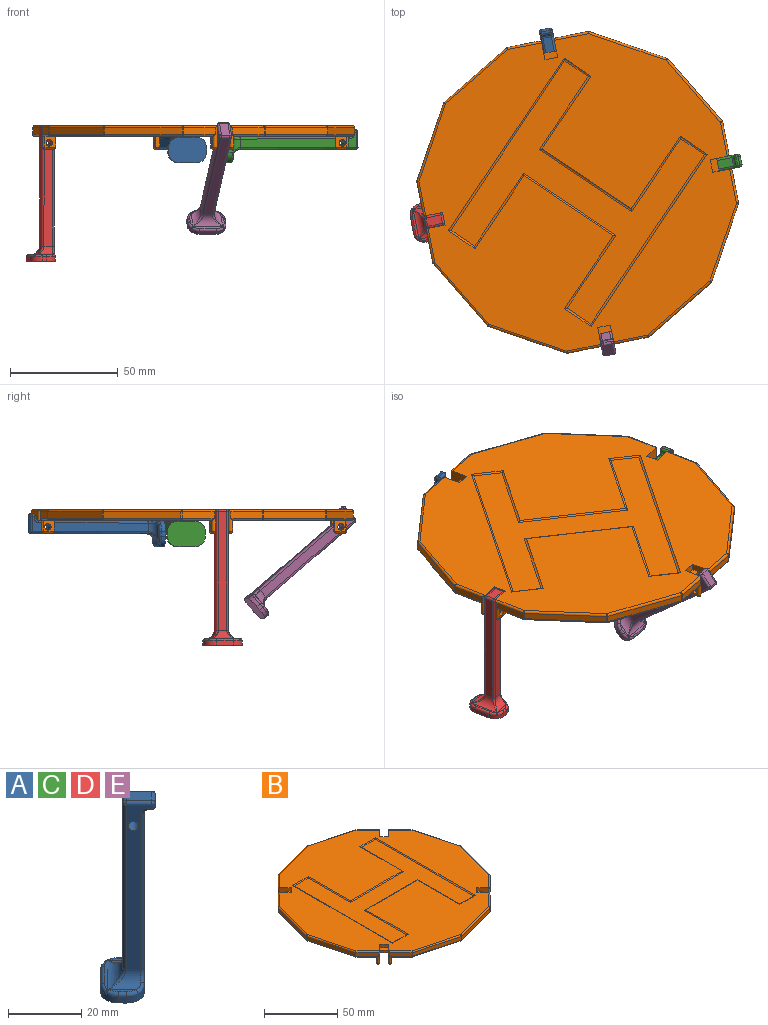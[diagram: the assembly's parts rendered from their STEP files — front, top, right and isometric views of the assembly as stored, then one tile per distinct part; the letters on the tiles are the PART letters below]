
ASSEMBLY  parts=5 mates=4
PART A: 63 faces, bbox 17.9x17.9x63 mm
  f0: plane 9.4x9.4mm, normal (0,0,1), area 11.6mm2, adj f20,f30,f34,f40
  f1: plane 5.16x5.16mm, normal (0,0,1), area 5.6mm2, adj f21,f54,f57,f59
  f2: plane 3.54x3.54mm, normal (0,0,-1), area 4mm2, adj f48,f49,f55,f56
  f3: plane 55x4.95mm, normal (-0.71,-0.71,0), area 216.8mm2, adj f9,f21,f36,f41,f47,f55,f58,f60
  f4: plane 7.78x7.78mm, normal (0,0,1), area 28mm2, adj f28,f31,f36,f37
  f5: plane 2.83x2.83mm, normal (0.71,-0.71,0), area 4mm2, adj f37,f38,f47,f48
  f6: plane 55x4.95mm, normal (0.71,0.71,0), area 216.8mm2, adj f9,f19,f24,f28,f38,f49,f50,f53
  f7: plane 55x2.83mm, normal (-0.71,0.71,0), area 220mm2, adj f20,f24,f31,f41
  f8: plane 59x5.66mm, normal (0.71,-0.71,0), area 252.8mm2, adj f10,f16,f17,f44,f50,f56,f60,f62
  f9: cylinder r=1.5mm len=6.36mm, axis (-0.71,-0.71,0), area 56.5mm2, adj f3,f6
  f10: cylinder r=5mm len=7.07mm, axis (0,0,1), area 17.8mm2, adj f8,f11,f17,f59,f61
  f11: plane 2x1.41mm, normal (-0.71,-0.71,0), area 4mm2, adj f10,f12,f17,f57
  f12: cylinder r=5mm len=7.07mm, axis (0,0,1), area 15.7mm2, adj f11,f13,f17,f40,f45,f51,f54
  f13: plane 5.66x5.66mm, normal (-0.71,0.71,0), area 16mm2, adj f12,f14,f17,f34
  f14: cylinder r=5mm len=7.07mm, axis (0,0,1), area 15.7mm2, adj f13,f15,f17,f22,f25,f26,f30
  f15: plane 2x1.41mm, normal (0.71,0.71,0), area 4mm2, adj f14,f16,f17,f29
  f16: cylinder r=5mm len=7.07mm, axis (0,0,1), area 17.8mm2, adj f8,f15,f17,f33,f39
  f17: plane 17.07x17.07mm, normal (0,0,-1), area 194.5mm2, adj f8,f10,f11,f12,f13,f14,f15,f16
  f18: plane 5.16x5.16mm, normal (0,0,1), area 5.6mm2, adj f19,f25,f29,f33
  f19: cylinder r=4mm len=9.07mm, axis (0.71,-0.71,0), area 35.5mm2, adj f6,f18,f22,f23,f39,f44
  f20: cylinder r=4mm len=12.49mm, axis (0.71,0.71,0), area 47.9mm2, adj f0,f7,f23,f26,f45,f46
  f21: cylinder r=4mm len=9.07mm, axis (-0.71,0.71,0), area 35.5mm2, adj f1,f3,f46,f51,f61,f62
  f22: bspline ~1.31x1.14mm, area 0.4mm2, adj f14,f19,f23,f25,f26
  f23: bspline ~6.36x4.13mm, area 7.1mm2, adj f19,f20,f22,f24,f26
  f24: cylinder r=1mm len=55mm, axis (0,0,1), area 86.4mm2, adj f6,f7,f23,f27
  f25: torus R=4mm, axis (0,0,-1), area 5.3mm2, adj f14,f18,f22,f29
  f26: bspline ~2.07x1.24mm, area 0.5mm2, adj f14,f20,f22,f23,f30
  f27: sphere r=1mm, area 1.9mm2, adj f24,f28,f31
  f28: cylinder r=1mm len=5.66mm, axis (-0.71,0.71,0), area 11mm2, adj f4,f6,f27,f32
  f29: cylinder r=1mm len=2.12mm, axis (0.71,-0.71,0), area 3.1mm2, adj f15,f18,f25,f33
  f30: torus R=4mm, axis (0,0,-1), area 5.3mm2, adj f0,f14,f26,f34
  f31: cylinder r=1mm len=3.54mm, axis (-0.71,-0.71,0), area 6.3mm2, adj f4,f7,f27,f35
  f32: sphere r=1mm, area 1.6mm2, adj f28,f37,f38
  f33: torus R=4mm, axis (0,0,-1), area 5.3mm2, adj f16,f18,f29,f39
  f34: cylinder r=1mm len=6.36mm, axis (0.71,0.71,0), area 12.6mm2, adj f0,f13,f30,f40
  f35: sphere r=1mm, area 1mm2, adj f31,f36,f41
  f36: cylinder r=1mm len=5.66mm, axis (0.71,-0.71,0), area 11mm2, adj f3,f4,f35,f42
  f37: cylinder r=1mm len=3.54mm, axis (0.71,0.71,0), area 6.3mm2, adj f4,f5,f32,f42
  f38: cylinder r=1mm len=1.41mm, axis (0,0,-1), area 1.6mm2, adj f5,f6,f32,f43
  f39: bspline ~5.56x2.46mm, area 5.6mm2, adj f16,f19,f33,f44
  f40: torus R=4mm, axis (0,0,-1), area 5.3mm2, adj f0,f12,f34,f45
  f41: cylinder r=1mm len=55mm, axis (0,0,-1), area 86.4mm2, adj f3,f7,f35,f46
  f42: sphere r=1mm, area 1.6mm2, adj f36,f37,f47
  f43: sphere r=1mm, area 1.3mm2, adj f38,f48,f49
  f44: torus R=5mm, axis (-0.71,0.71,0), area 6.4mm2, adj f8,f19,f39,f50
  f45: bspline ~1.31x1.14mm, area 0.4mm2, adj f12,f20,f40,f46,f51
  f46: bspline ~6.36x4.13mm, area 7.1mm2, adj f20,f21,f41,f45,f51
  f47: cylinder r=1mm len=1.41mm, axis (0,0,1), area 1.6mm2, adj f3,f5,f42,f52
  f48: cylinder r=1mm len=3.54mm, axis (0.71,0.71,0), area 6.3mm2, adj f2,f5,f43,f52
  f49: cylinder r=1mm len=1.41mm, axis (-0.71,0.71,0), area 1.6mm2, adj f2,f6,f43,f53
  f50: cylinder r=1mm len=52mm, axis (0,0,1), area 81.7mm2, adj f6,f8,f44,f53
  f51: bspline ~2.07x1.24mm, area 0.5mm2, adj f12,f21,f45,f46,f54
  f52: sphere r=1mm, area 1mm2, adj f47,f48,f55
  f53: torus R=2mm, axis (-0.71,-0.71,0), area 3.4mm2, adj f6,f49,f50,f56
  f54: torus R=4mm, axis (0,0,-1), area 5.3mm2, adj f1,f12,f51,f57
  f55: cylinder r=1mm len=1.41mm, axis (0.71,-0.71,0), area 1.6mm2, adj f2,f3,f52,f58
  f56: cylinder r=1mm len=3.54mm, axis (-0.71,-0.71,0), area 6.3mm2, adj f2,f8,f53,f58
  f57: cylinder r=1mm len=2.12mm, axis (-0.71,0.71,0), area 3.1mm2, adj f1,f11,f54,f59
  f58: torus R=2mm, axis (-0.71,-0.71,0), area 3.4mm2, adj f3,f55,f56,f60
  f59: torus R=4mm, axis (0,0,-1), area 5.3mm2, adj f1,f10,f57,f61
  f60: cylinder r=1mm len=52mm, axis (0,0,-1), area 81.7mm2, adj f3,f8,f58,f62
  f61: bspline ~5.56x2.46mm, area 5.6mm2, adj f10,f21,f59,f62
  f62: torus R=5mm, axis (-0.71,0.71,0), area 6.4mm2, adj f8,f21,f60,f61
PART B: 175 faces, bbox 149.9x149.9x11 mm
  f0: plane 147.93x147.93mm, normal (0,0,-1), area 16212.3mm2, adj f20,f22,f25,f28,f39,f40,f41,f42
  f1: plane 147.93x147.93mm, normal (0,0,1), area 12571.8mm2, adj f19,f21,f23,f24,f26,f27,f29,f30
  f2: plane 10.71x10.71mm, normal (0.71,0.71,0), area 45.4mm2, adj f116,f117,f119,f120
  f3: plane 10.71x10.71mm, normal (-0.71,0.71,0), area 45.4mm2, adj f141,f142,f144,f145
  f4: plane 10.71x10.71mm, normal (-0.71,-0.71,0), area 45.4mm2, adj f82,f83,f86,f87
  f5: plane 10.71x10.71mm, normal (0.71,-0.71,0), area 45.4mm2, adj f91,f92,f94,f95
  f6: plane 36.98x9.91mm, normal (0.97,-0.26,0), area 114.9mm2, adj f124,f126,f131,f132
  f7: plane 36.98x9.91mm, normal (0.97,0.26,0), area 114.9mm2, adj f119,f121,f124,f125
  f8: plane 10.71x10.71mm, normal (0.71,0.71,0), area 45.4mm2, adj f156,f159,f161,f162
  f9: plane 36.98x9.91mm, normal (0.26,0.97,0), area 114.9mm2, adj f149,f151,f156,f157
  f10: plane 36.98x9.91mm, normal (-0.26,0.97,0), area 114.9mm2, adj f144,f146,f149,f150
  f11: plane 10.71x10.71mm, normal (-0.71,0.71,0), area 45.4mm2, adj f66,f67,f69,f70
  f12: plane 36.98x9.91mm, normal (-0.97,0.26,0), area 114.9mm2, adj f70,f71,f74,f75
  f13: plane 36.98x9.91mm, normal (-0.97,-0.26,0), area 114.9mm2, adj f75,f76,f81,f82
  f14: plane 10.71x10.71mm, normal (-0.71,-0.71,0), area 45.4mm2, adj f106,f109,f111,f112
  f15: plane 36.98x9.91mm, normal (-0.26,-0.97,0), area 114.9mm2, adj f99,f101,f106,f107
  f16: plane 36.98x9.91mm, normal (0.26,-0.97,0), area 114.9mm2, adj f94,f96,f99,f100
  f17: plane 10.71x10.71mm, normal (0.71,-0.71,0), area 45.4mm2, adj f131,f134,f136,f137
  f18: plane 94.89x78.27mm, normal (0,0,1), area 3204.3mm2, adj f163,f164,f165,f166,f167,f168,f169,f170
  f19: plane 10x5.66mm, normal (0.71,0.71,0), area 51.9mm2, adj f1,f20,f31,f32,f40,f56,f64,f66
  f20: plane 4.24x4.24mm, normal (-0.71,0.71,0), area 12mm2, adj f0,f19,f21,f32
  f21: plane 10x5.66mm, normal (-0.71,-0.71,0), area 51.9mm2, adj f1,f20,f31,f32,f41,f55,f138,f141
  f22: plane 4.24x4.24mm, normal (0.71,0.71,0), area 12mm2, adj f0,f23,f24,f34
  f23: plane 10x5.66mm, normal (-0.71,0.71,0), area 51.9mm2, adj f1,f22,f33,f34,f53,f61,f113,f116
  f24: plane 10x5.66mm, normal (0.71,-0.71,0), area 51.9mm2, adj f1,f22,f33,f34,f52,f62,f154,f161
  f25: plane 4.24x4.24mm, normal (0.71,-0.71,0), area 12mm2, adj f0,f26,f27,f36
  f26: plane 10x5.66mm, normal (0.71,0.71,0), area 51.9mm2, adj f1,f25,f35,f36,f49,f59,f88,f91
  f27: plane 10x5.66mm, normal (-0.71,-0.71,0), area 51.9mm2, adj f1,f25,f35,f36,f48,f60,f129,f136
  f28: plane 4.24x4.24mm, normal (-0.71,-0.71,0), area 12mm2, adj f0,f29,f30,f38
  f29: plane 10x5.66mm, normal (0.71,-0.71,0), area 51.9mm2, adj f1,f28,f37,f38,f45,f57,f79,f86
  f30: plane 10x5.66mm, normal (-0.71,0.71,0), area 51.9mm2, adj f1,f28,f37,f38,f44,f58,f104,f111
  f31: plane 4.24x4.24mm, normal (-0.71,0.71,0), area 18mm2, adj f1,f19,f21,f32
  f32: plane 6.36x6.36mm, normal (0,0,1), area 18mm2, adj f19,f20,f21,f31
  f33: plane 4.24x4.24mm, normal (0.71,0.71,0), area 18mm2, adj f1,f23,f24,f34
  f34: plane 6.36x6.36mm, normal (0,0,1), area 18mm2, adj f22,f23,f24,f33
  f35: plane 4.24x4.24mm, normal (0.71,-0.71,0), area 18mm2, adj f1,f26,f27,f36
  f36: plane 6.36x6.36mm, normal (0,0,1), area 18mm2, adj f25,f26,f27,f35
  f37: plane 4.24x4.24mm, normal (-0.71,-0.71,0), area 18mm2, adj f1,f29,f30,f38
  f38: plane 6.36x6.36mm, normal (0,0,1), area 18mm2, adj f28,f29,f30,f37
  f39: plane 5x3.54mm, normal (-0.71,-0.71,0), area 17.9mm2, adj f0,f40,f56,f64,f66
  f40: plane 5x1.41mm, normal (0.71,-0.71,0), area 10mm2, adj f0,f19,f39,f63
  f41: plane 5x1.41mm, normal (0.71,-0.71,0), area 10mm2, adj f0,f21,f42,f139
  f42: plane 5x3.54mm, normal (0.71,0.71,0), area 17.9mm2, adj f0,f41,f55,f138,f141
  f43: plane 5x3.54mm, normal (0.71,-0.71,0), area 17.9mm2, adj f0,f44,f58,f104,f111
  f44: plane 5x1.41mm, normal (0.71,0.71,0), area 10mm2, adj f0,f30,f43,f103
  f45: plane 5x1.41mm, normal (0.71,0.71,0), area 10mm2, adj f0,f29,f46,f80
  f46: plane 5x3.54mm, normal (-0.71,0.71,0), area 17.9mm2, adj f0,f45,f57,f79,f86
  f47: plane 5x3.54mm, normal (0.71,0.71,0), area 17.9mm2, adj f0,f48,f60,f129,f136
  f48: plane 5x1.41mm, normal (-0.71,0.71,0), area 10mm2, adj f0,f27,f47,f128
  f49: plane 5x1.41mm, normal (-0.71,0.71,0), area 10mm2, adj f0,f26,f50,f89
  f50: plane 5x3.54mm, normal (-0.71,-0.71,0), area 17.9mm2, adj f0,f49,f59,f88,f91
  f51: plane 5x3.54mm, normal (-0.71,0.71,0), area 17.9mm2, adj f0,f52,f62,f154,f161
  f52: plane 5x1.41mm, normal (-0.71,-0.71,0), area 10mm2, adj f0,f24,f51,f153
  f53: plane 5x1.41mm, normal (-0.71,-0.71,0), area 10mm2, adj f0,f23,f54,f114
  f54: plane 5x3.54mm, normal (0.71,-0.71,0), area 17.9mm2, adj f0,f53,f61,f113,f116
  f55: cylinder r=1.5mm len=3.54mm, axis (-0.71,-0.71,0), area 18.8mm2, adj f21,f42
  f56: cylinder r=1.5mm len=3.54mm, axis (-0.71,-0.71,0), area 18.8mm2, adj f19,f39
  f57: cylinder r=1.5mm len=3.54mm, axis (0.71,-0.71,0), area 18.8mm2, adj f29,f46
  f58: cylinder r=1.5mm len=3.54mm, axis (0.71,-0.71,0), area 18.8mm2, adj f30,f43
  f59: cylinder r=1.5mm len=3.54mm, axis (0.71,0.71,0), area 18.8mm2, adj f26,f50
  f60: cylinder r=1.5mm len=3.54mm, axis (0.71,0.71,0), area 18.8mm2, adj f27,f47
  f61: cylinder r=1.5mm len=3.54mm, axis (-0.71,0.71,0), area 18.8mm2, adj f23,f54
  f62: cylinder r=1.5mm len=3.54mm, axis (-0.71,0.71,0), area 18.8mm2, adj f24,f51
  f63: cylinder r=1mm len=2.12mm, axis (-0.71,-0.71,0), area 2mm2, adj f40,f64
  f64: cylinder r=1mm len=4.95mm, axis (0.71,-0.71,0), area 14.6mm2, adj f19,f39,f63,f65
  f65: sphere r=1mm, area 3.1mm2, adj f64,f66
  f66: cylinder r=1mm len=10mm, axis (0,0,-1), area 23.6mm2, adj f11,f19,f39,f65,f67,f69
  f67: cylinder r=1mm len=12.12mm, axis (0.71,0.71,0), area 24.8mm2, adj f1,f11,f66,f68
  f68: sphere r=1mm, area 0.5mm2, adj f67,f70,f71
  f69: cylinder r=1mm len=11.42mm, axis (-0.71,-0.71,0), area 22.8mm2, adj f0,f11,f66,f72
  f70: cylinder r=1mm len=3mm, axis (0,0,-1), area 1.6mm2, adj f11,f12,f68,f72
  f71: cylinder r=1mm len=37.24mm, axis (0.26,0.97,0), area 60.1mm2, adj f1,f12,f68,f73
  f72: sphere r=1mm, area 0.5mm2, adj f69,f70,f74
  f73: sphere r=1mm, area 0.5mm2, adj f71,f75,f76
  f74: cylinder r=1mm len=37.24mm, axis (-0.26,-0.97,0), area 60.1mm2, adj f0,f12,f72,f77
  f75: cylinder r=1mm len=3mm, axis (0,0,-1), area 1.6mm2, adj f12,f13,f73,f77
  f76: cylinder r=1mm len=37.24mm, axis (-0.26,0.97,0), area 60.1mm2, adj f1,f13,f73,f78
  f77: sphere r=1mm, area 0.5mm2, adj f74,f75,f81
  f78: sphere r=1mm, area 0.5mm2, adj f76,f82,f83
  f79: cylinder r=1mm len=4.95mm, axis (-0.71,-0.71,0), area 14.6mm2, adj f29,f46,f80,f84
  f80: cylinder r=1mm len=2.12mm, axis (0.71,-0.71,0), area 2mm2, adj f45,f79
  f81: cylinder r=1mm len=37.24mm, axis (0.26,-0.97,0), area 60.1mm2, adj f0,f13,f77,f85
  f82: cylinder r=1mm len=3mm, axis (0,0,-1), area 1.6mm2, adj f4,f13,f78,f85
  f83: cylinder r=1mm len=12.12mm, axis (-0.71,0.71,0), area 24.8mm2, adj f1,f4,f78,f86
  f84: sphere r=1mm, area 3.1mm2, adj f79,f86
  f85: sphere r=1mm, area 0.5mm2, adj f81,f82,f87
  f86: cylinder r=1mm len=10mm, axis (0,0,1), area 23.6mm2, adj f4,f29,f46,f83,f84,f87
  f87: cylinder r=1mm len=11.42mm, axis (0.71,-0.71,0), area 22.8mm2, adj f0,f4,f85,f86
  f88: cylinder r=1mm len=4.95mm, axis (0.71,-0.71,0), area 14.6mm2, adj f26,f50,f89,f90
  f89: cylinder r=1mm len=2.12mm, axis (0.71,0.71,0), area 2mm2, adj f49,f88
  f90: sphere r=1mm, area 3.1mm2, adj f88,f91
  f91: cylinder r=1mm len=10mm, axis (0,0,1), area 23.6mm2, adj f5,f26,f50,f90,f92,f95
  f92: cylinder r=1mm len=12.12mm, axis (-0.71,-0.71,0), area 24.8mm2, adj f1,f5,f91,f93
  f93: sphere r=1mm, area 0.5mm2, adj f92,f94,f96
  f94: cylinder r=1mm len=3mm, axis (0,0,-1), area 1.6mm2, adj f5,f16,f93,f97
  f95: cylinder r=1mm len=11.42mm, axis (0.71,0.71,0), area 22.8mm2, adj f0,f5,f91,f97
  f96: cylinder r=1mm len=37.24mm, axis (-0.97,-0.26,0), area 60.1mm2, adj f1,f16,f93,f98
  f97: sphere r=1mm, area 0.5mm2, adj f94,f95,f100
  f98: sphere r=1mm, area 0.5mm2, adj f96,f99,f101
  f99: cylinder r=1mm len=3mm, axis (0,0,-1), area 1.6mm2, adj f15,f16,f98,f102
  f100: cylinder r=1mm len=37.24mm, axis (0.97,0.26,0), area 60.1mm2, adj f0,f16,f97,f102
  f101: cylinder r=1mm len=37.24mm, axis (-0.97,0.26,0), area 60.1mm2, adj f1,f15,f98,f105
  f102: sphere r=1mm, area 0.5mm2, adj f99,f100,f107
  f103: cylinder r=1mm len=2.12mm, axis (0.71,-0.71,0), area 2mm2, adj f44,f104
  f104: cylinder r=1mm len=4.95mm, axis (0.71,0.71,0), area 14.6mm2, adj f30,f43,f103,f108
  f105: sphere r=1mm, area 0.5mm2, adj f101,f106,f109
  f106: cylinder r=1mm len=3mm, axis (0,0,-1), area 1.6mm2, adj f14,f15,f105,f110
  f107: cylinder r=1mm len=37.24mm, axis (0.97,-0.26,0), area 60.1mm2, adj f0,f15,f102,f110
  f108: sphere r=1mm, area 3.1mm2, adj f104,f111
  f109: cylinder r=1mm len=12.12mm, axis (-0.71,0.71,0), area 24.8mm2, adj f1,f14,f105,f111
  f110: sphere r=1mm, area 0.5mm2, adj f106,f107,f112
  f111: cylinder r=1mm len=10mm, axis (0,0,-1), area 23.6mm2, adj f14,f30,f43,f108,f109,f112
  f112: cylinder r=1mm len=11.42mm, axis (0.71,-0.71,0), area 22.8mm2, adj f0,f14,f110,f111
  f113: cylinder r=1mm len=4.95mm, axis (0.71,0.71,0), area 14.6mm2, adj f23,f54,f114,f115
  f114: cylinder r=1mm len=2.12mm, axis (-0.71,0.71,0), area 2mm2, adj f53,f113
  f115: sphere r=1mm, area 3.1mm2, adj f113,f116
  f116: cylinder r=1mm len=10mm, axis (0,0,1), area 23.6mm2, adj f2,f23,f54,f115,f117,f120
  f117: cylinder r=1mm len=12.12mm, axis (0.71,-0.71,0), area 24.8mm2, adj f1,f2,f116,f118
  f118: sphere r=1mm, area 0.5mm2, adj f117,f119,f121
  f119: cylinder r=1mm len=3mm, axis (0,0,-1), area 1.6mm2, adj f2,f7,f118,f122
  f120: cylinder r=1mm len=11.42mm, axis (-0.71,0.71,0), area 22.8mm2, adj f0,f2,f116,f122
  f121: cylinder r=1mm len=37.24mm, axis (0.26,-0.97,0), area 60.1mm2, adj f1,f7,f118,f123
  f122: sphere r=1mm, area 0.5mm2, adj f119,f120,f125
  f123: sphere r=1mm, area 0.5mm2, adj f121,f124,f126
  f124: cylinder r=1mm len=3mm, axis (0,0,-1), area 1.6mm2, adj f6,f7,f123,f127
  f125: cylinder r=1mm len=37.24mm, axis (-0.26,0.97,0), area 60.1mm2, adj f0,f7,f122,f127
  f126: cylinder r=1mm len=37.24mm, axis (-0.26,-0.97,0), area 60.1mm2, adj f1,f6,f123,f130
  f127: sphere r=1mm, area 0.5mm2, adj f124,f125,f132
  f128: cylinder r=1mm len=2.12mm, axis (0.71,0.71,0), area 2mm2, adj f48,f129
  f129: cylinder r=1mm len=4.95mm, axis (-0.71,0.71,0), area 14.6mm2, adj f27,f47,f128,f133
  f130: sphere r=1mm, area 0.5mm2, adj f126,f131,f134
  f131: cylinder r=1mm len=3mm, axis (0,0,-1), area 1.6mm2, adj f6,f17,f130,f135
  f132: cylinder r=1mm len=37.24mm, axis (0.26,0.97,0), area 60.1mm2, adj f0,f6,f127,f135
  f133: sphere r=1mm, area 3.1mm2, adj f129,f136
  f134: cylinder r=1mm len=12.12mm, axis (-0.71,-0.71,0), area 24.8mm2, adj f1,f17,f130,f136
  f135: sphere r=1mm, area 0.5mm2, adj f131,f132,f137
  f136: cylinder r=1mm len=10mm, axis (0,0,-1), area 23.6mm2, adj f17,f27,f47,f133,f134,f137
  f137: cylinder r=1mm len=11.42mm, axis (0.71,0.71,0), area 22.8mm2, adj f0,f17,f135,f136
  f138: cylinder r=1mm len=4.95mm, axis (-0.71,0.71,0), area 14.6mm2, adj f21,f42,f139,f140
  f139: cylinder r=1mm len=2.12mm, axis (-0.71,-0.71,0), area 2mm2, adj f41,f138
  f140: sphere r=1mm, area 3.1mm2, adj f138,f141
  f141: cylinder r=1mm len=10mm, axis (0,0,1), area 23.6mm2, adj f3,f21,f42,f140,f142,f145
  f142: cylinder r=1mm len=12.12mm, axis (0.71,0.71,0), area 24.8mm2, adj f1,f3,f141,f143
  f143: sphere r=1mm, area 0.5mm2, adj f142,f144,f146
  f144: cylinder r=1mm len=3mm, axis (0,0,-1), area 1.6mm2, adj f3,f10,f143,f147
  f145: cylinder r=1mm len=11.42mm, axis (-0.71,-0.71,0), area 22.8mm2, adj f0,f3,f141,f147
  f146: cylinder r=1mm len=37.24mm, axis (0.97,0.26,0), area 60.1mm2, adj f1,f10,f143,f148
  f147: sphere r=1mm, area 0.5mm2, adj f144,f145,f150
  f148: sphere r=1mm, area 0.5mm2, adj f146,f149,f151
  f149: cylinder r=1mm len=3mm, axis (0,0,-1), area 1.6mm2, adj f9,f10,f148,f152
  f150: cylinder r=1mm len=37.24mm, axis (-0.97,-0.26,0), area 60.1mm2, adj f0,f10,f147,f152
  f151: cylinder r=1mm len=37.24mm, axis (0.97,-0.26,0), area 60.1mm2, adj f1,f9,f148,f155
  f152: sphere r=1mm, area 0.5mm2, adj f149,f150,f157
  f153: cylinder r=1mm len=2.12mm, axis (-0.71,0.71,0), area 2mm2, adj f52,f154
  f154: cylinder r=1mm len=4.95mm, axis (-0.71,-0.71,0), area 14.6mm2, adj f24,f51,f153,f158
  f155: sphere r=1mm, area 0.5mm2, adj f151,f156,f159
  f156: cylinder r=1mm len=3mm, axis (0,0,-1), area 1.6mm2, adj f8,f9,f155,f160
  f157: cylinder r=1mm len=37.24mm, axis (-0.97,0.26,0), area 60.1mm2, adj f0,f9,f152,f160
  f158: sphere r=1mm, area 3.1mm2, adj f154,f161
  f159: cylinder r=1mm len=12.12mm, axis (0.71,-0.71,0), area 24.8mm2, adj f1,f8,f155,f161
  f160: sphere r=1mm, area 0.5mm2, adj f156,f157,f162
  f161: cylinder r=1mm len=10mm, axis (0,0,-1), area 23.6mm2, adj f8,f24,f51,f158,f159,f162
  f162: cylinder r=1mm len=11.42mm, axis (-0.71,0.71,0), area 22.8mm2, adj f0,f8,f160,f161
  f163: cylinder r=1mm len=51.73mm, axis (-1,0,0), area 53.2mm2, adj f1,f18,f164,f165
  f164: cylinder r=1mm len=41.68mm, axis (0,1,0), area 42.7mm2, adj f1,f18,f163,f166
  f165: cylinder r=1mm len=41.68mm, axis (0,1,0), area 42.7mm2, adj f1,f18,f163,f167
  f166: cylinder r=1mm len=15mm, axis (-1,0,0), area 14.9mm2, adj f1,f18,f164,f168
  f167: cylinder r=1mm len=15mm, axis (1,0,0), area 14.9mm2, adj f1,f18,f165,f169
  f168: cylinder r=1mm len=96.62mm, axis (0,-1,0), area 100.4mm2, adj f1,f18,f166,f170
  f169: cylinder r=1mm len=96.62mm, axis (0,-1,0), area 100.4mm2, adj f1,f18,f167,f171
  f170: cylinder r=1mm len=15mm, axis (1,0,0), area 14.9mm2, adj f1,f18,f168,f172
  f171: cylinder r=1mm len=15mm, axis (-1,0,0), area 14.9mm2, adj f1,f18,f169,f173
  f172: cylinder r=1mm len=41.68mm, axis (0,1,0), area 42.7mm2, adj f1,f18,f170,f174
  f173: cylinder r=1mm len=41.68mm, axis (0,1,0), area 42.7mm2, adj f1,f18,f171,f174
  f174: cylinder r=1mm len=51.73mm, axis (1,0,0), area 53.2mm2, adj f1,f18,f172,f173
PART C: same geometry as A
PART D: same geometry as A
PART E: same geometry as A
PLACE A rot(axis=(-0.85,-0.45,-0.28),94.6deg) t=(-49.82,30.41,84.34)mm
PLACE B rot(axis=(0,0,-1),33.9deg) t=(-35.9,-40.29,17.88)mm fixed
PLACE C rot(axis=(-0.72,0.22,-0.66),141deg) t=(34.86,-26.35,84.34)mm
PLACE D rot(axis=(0,0,1),56.1deg) t=(-35.89,-40.29,17.72)mm
PLACE E rot(axis=(0.2,-0.38,0.9),149.3deg) t=(-30.73,-66.54,69.73)mm
MATE revolute E.f9 <-> B.f59  axis (0.98,0.19,0) through (-19.54,-107.84,14.88)mm
MATE revolute C.f9 <-> B.f61  axis (-0.19,0.98,0) through (32.82,-29.81,14.88)mm
MATE revolute A.f9 <-> B.f55  axis (-0.98,-0.19,0) through (-52.26,27.27,14.88)mm
MATE revolute D.f9 <-> B.f57  axis (0.19,-0.98,0) through (-103.46,-56.65,14.88)mm
